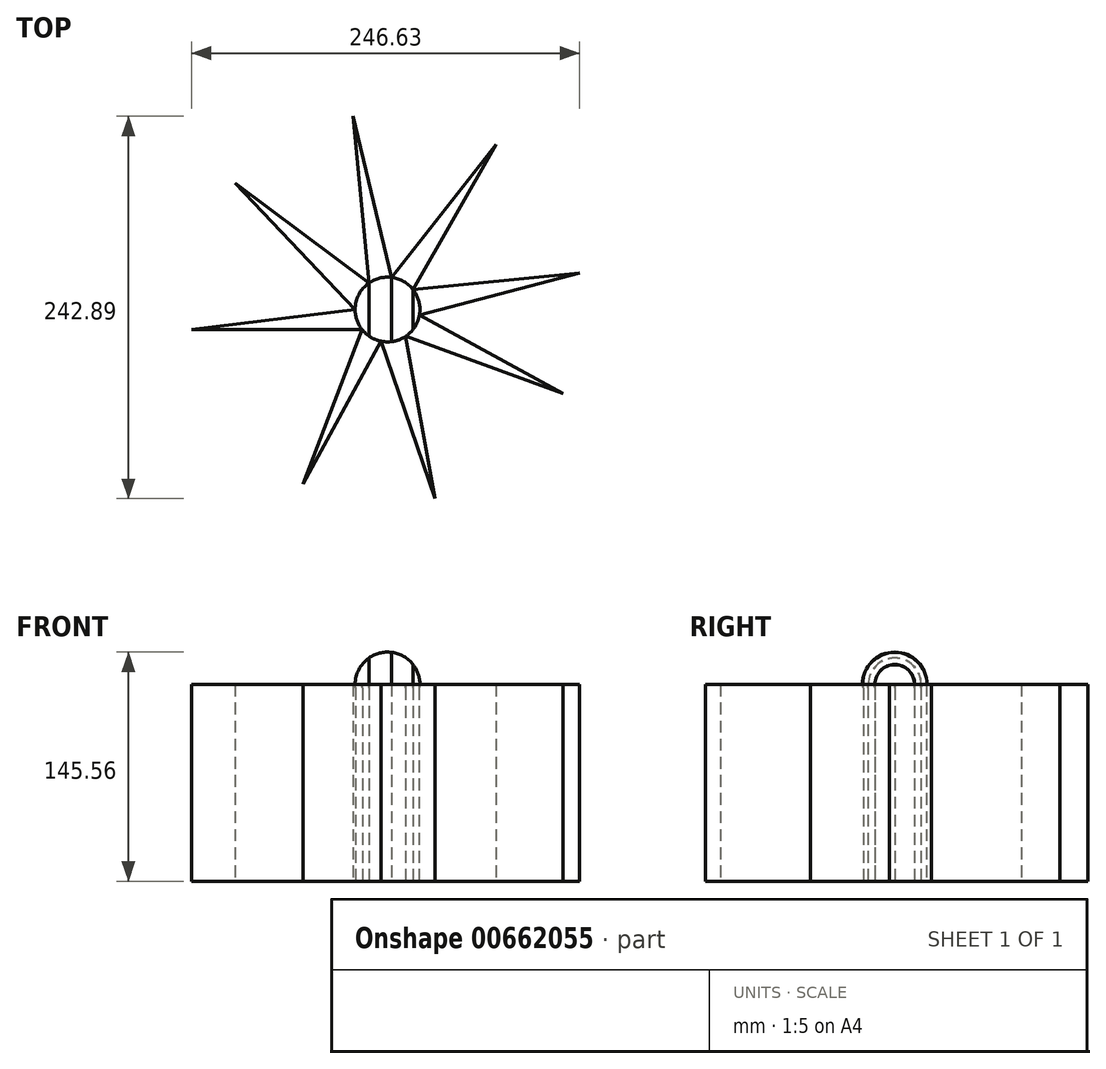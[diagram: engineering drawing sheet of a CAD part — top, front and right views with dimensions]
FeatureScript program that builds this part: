
annotation { "Feature Type Name" : "Feature", "Feature Type Description" : "" }
export const myFeature = defineFeature(function(context is Context, id is Id, definition is map)
    precondition{}
    {
        {
            var Q0;
            Q0=qCreatedBy(makeId("Top.planeOp"),FACE);
            var sketch = newSketch(context, id + "F0", { "sketchPlane" : qUnion([Q0])});
            skCircle(sketch, "E0", {"center": v(0, 0) * mm, "radius": 125 * mm});
            skSolve(sketch);
        }
        {
            var Q0;
            Q0=makeQuery(id+"F0.imprint","IMPRINT",FACE,{"disambiguationData":[TD([[makeQuery(id+"F0.imprint","IMPRINT",EDGE,{"derivedFrom":sQuery(id+"F0.wireOp",EDGE,"E0")}),1.0]])]});
            var sketch = newSketch(context, id + "F1", { "sketchPlane" : qUnion([Q0])});
            skCircle(sketch, "E1", {"center": v(0, 0) * mm, "radius": 20.43 * mm});
            skLineSegment(sketch, "E2", {"start": v(-11.76, 16.7) * mm, "end": v(-21.93, 122.78) * mm});
            skLineSegment(sketch, "E3", {"start": v(-21.93, 122.78) * mm, "end": v(2.6, 20.27) * mm});
            skLineSegment(sketch, "E4", {"start": v(2.6, 20.27) * mm, "end": v(69.02, 104.85) * mm});
            skLineSegment(sketch, "E5", {"start": v(69.02, 104.85) * mm, "end": v(16.12, 12.56) * mm});
            skLineSegment(sketch, "E6", {"start": v(16.12, 12.56) * mm, "end": v(122.04, 23.28) * mm});
            skLineSegment(sketch, "E7", {"start": v(122.04, 23.28) * mm, "end": v(20.14, -3.46) * mm});
            skLineSegment(sketch, "E8", {"start": v(20.14, -3.46) * mm, "end": v(111.42, -53.4) * mm});
            skLineSegment(sketch, "E9", {"start": v(111.42, -53.4) * mm, "end": v(11.44, -16.93) * mm});
            skLineSegment(sketch, "E10", {"start": v(11.44, -16.93) * mm, "end": v(30.1, -120.11) * mm});
            skLineSegment(sketch, "E11", {"start": v(30.1, -120.11) * mm, "end": v(-4.06, -20.03) * mm});
            skLineSegment(sketch, "E12", {"start": v(-4.06, -20.03) * mm, "end": v(-53.66, -110.7) * mm});
            skLineSegment(sketch, "E13", {"start": v(-53.66, -110.7) * mm, "end": v(-16.02, -12.69) * mm});
            skLineSegment(sketch, "E14", {"start": v(-16.02, -12.69) * mm, "end": v(-124.59, -12.69) * mm});
            skLineSegment(sketch, "E15", {"start": v(-124.59, -12.69) * mm, "end": v(-20.43, 0) * mm});
            skLineSegment(sketch, "E16", {"start": v(-20.43, 0) * mm, "end": v(-96.7, 80.38) * mm});
            skLineSegment(sketch, "E17", {"start": v(-96.7, 80.38) * mm, "end": v(-11.76, 16.7) * mm});
            skSolve(sketch);
        }
        {
            var Q0;
            Q0 = qSketchRegion(id + "F1", true);
            extrude(context, id + "F2", {"entities" : qUnion([Q0]), "depth" : 125 * mm, "offsetDistance" : 25 * mm});
        }
        {
            var Q0;
            Q0=makeQuery(id+"F2.opExtrude","CAP_FACE",FACE,{"disambiguationData":[OSD([sQuery(id+"F1.wireOp",EDGE,"E2"),sQuery(id+"F1.wireOp",EDGE,"E3"),sQuery(id+"F1.wireOp",EDGE,"E4"),sQuery(id+"F1.wireOp",EDGE,"E5"),sQuery(id+"F1.wireOp",EDGE,"E6"),sQuery(id+"F1.wireOp",EDGE,"E7"),sQuery(id+"F1.wireOp",EDGE,"E8"),sQuery(id+"F1.wireOp",EDGE,"E9"),sQuery(id+"F1.wireOp",EDGE,"E10"),sQuery(id+"F1.wireOp",EDGE,"E11"),sQuery(id+"F1.wireOp",EDGE,"E12"),sQuery(id+"F1.wireOp",EDGE,"E13"),sQuery(id+"F1.wireOp",EDGE,"E14"),sQuery(id+"F1.wireOp",EDGE,"E15"),sQuery(id+"F1.wireOp",EDGE,"E16"),sQuery(id+"F1.wireOp",EDGE,"E17")])],"isStart":false});
            var sketch = newSketch(context, id + "F3", { "sketchPlane" : qUnion([Q0])});
            skCircle(sketch, "E18", {"center": v(0, 0) * mm, "radius": 20.56 * mm});
            skLineSegment(sketch, "E19", {"start": v(-20.43, 0) * mm, "end": v(20.56, 0) * mm});
            skSolve(sketch);
        }
        {
            var Q0;
            {var subQ13=sQuery(id+"F3.wireOp",EDGE,"E19");Q0=makeQuery(id+"F3.imprint","IMPRINT",FACE,{"disambiguationData":[TD([[makeQuery(id+"F3.imprint","IMPRINT",EDGE,{"derivedFrom":subQ13}),1.0]])]});}
            var Q1;
            Q1=sQuery(id+"F3.wireOp",EDGE,"E19");
            revolve(context, id + "F4", {"operationType" : NewBodyOperationType.ADD, "entities" : qUnion([Q0]), "axis" : qUnion([Q1]), "revolveType" : RevolveType.FULL});
        }
    });
